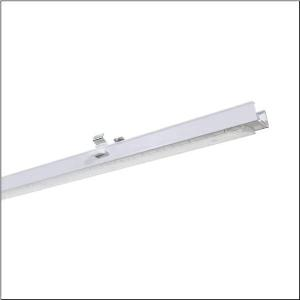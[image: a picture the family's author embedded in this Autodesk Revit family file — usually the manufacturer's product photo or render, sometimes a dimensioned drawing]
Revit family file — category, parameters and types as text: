
# Revit family: trunking_flex_31_51re12mb58b
name_source: partatom
category: Lighting Fixtures
units: mm (PartAtom-declared; Revit-internal decimal feet)

## family parameters
Cut with Voids When Loaded = No
Host = Face
Light Source = No
Part Type = Normal
Room Calculation Point = No
Round Connector Dimension = Use Diameter
Shared = No

## types (1)
- --- (1 x LED, 8000 lm, 50 W, 5000K)
    Apparent Load = 50 VA
    CIE Flux Codes = 65 91 98 99 100
    Color Rendering = 80
    Color Temperature = 5000K
    Default Elevation = 1800 mm
    Description = Trunking Flex 31, luminaire insert, of extruded aluminium section, coated, traffic white (RAL 9016), length: 1.472mm, width: 91mm, height: 53mm, LED rated luminous flux: 8.000lm, light colour: 850, control gear: ON/OFF Multilumen, with system connector: socket, mains connection: 220..240V, AC, 50/60Hz, rated input power: 50W, luminous flux adjustable on luminaire in four steps (4130/5610/6850/8000lm), connected load according to luminous flux setting (25/34/42/50W), primary light control with lens, of plastic, primary optical cover: cover, of PMMA, light emission: direct distribution, protection rating (complete): IP20, insulation class (complete): insulation class I (protective earthing), certification: CE, UKCA, impact resistance: IK02, permissible ambient temperature for indoor applications: -20..+40°C, packaging unit: 1 piece
    Height = 58 mm
    Lamp = 1 x LED
    Lamp Light Flux = 8000 lm
    Lamp Power = 50 W
    Lamp count = 1
    Length = 1472 mm
    Luminous efficacy = 160 lm/W
    Manufacturer = Siteco
    ModVariant = No
    Model = 51RE12MB58B
    Mounting Place = Ceiling
    Mounting Type = Pendant
    Number of Poles = 1
    OnlyDefault = Yes
    Power Factor = 1
    Product Name = Trunking Flex 31
    Product group = luminaire insert
    ProductGroupID = 901
    Protection Class = Protection class I
    Protection Degree = IP 20
    RLX_Detail_Level = 1
    RLX_Emergency_Light_Flux = 0 lm
    RLX_Emergency_Type = 0
    RLX_Emergency_Type_DB = No
    RlxData = <blob elided: 20309 chars, md5=ad110d7e>
    Socket = socket
    Standby Power = 0 W
    System Light Flux = 8000 lm
    System Power = 50 W
    Type Comments = factory setting: luminous flux: 100 % | (ON | ON) | 300 mA
    Type Image = l_1266702.jpg
    URL = http://relux.com
    VarID = @adj_018633
    Voltage = 0 V
    Weight = 0.00 kg
    Width = 65 mm

## geometry (parser evidence)
native form markers: Blend x4, Sweep x11
no freeform markers — native parametric forms only
